# Revit family: NBS_Senator_MeetingPods_EnclaveOne
name_source: partatom
category: Furniture
revit_build: Autodesk Revit 2018 (Build: 20190510_1515(x64)
units: mm (PartAtom-declared; Revit-internal decimal feet)

## family parameters
Always vertical = Yes
Cut with Voids When Loaded = No
Room Calculation Point = No
Shared = No
Work Plane-Based = No

## types (2) — shared parameters
Accessories = Monitor arms, PU desk accessories, desk top accessories, CPU holders, electrical accessories, coat hanger, name plate, A2 dry wipe board with hanger, A3 dry wipe board with hanger
AssetType = Fixed
Category = Pr_40_50_12_53:Meeting pods
DurationUnit = year
EnclaveOneDepth = 1000 mm  [stored 3.28084 ft]
EnclaveOneWidth = 1500 mm  [stored 4.92126 ft]
ExpectedLife = 10
FabricFinishOptions = Plymouth, fairfield, latymer, lancaster, silcoates, silverdale, st andrews, trevelyan, ulster, wellington, wesley, manchester,
Features = Internal frame with multi-layered acoustic foam, levelling adjusters, blazer fabric, outer vertical panels
Finish = Outer vertical panels upholstered in camira, blazer fabric Two tone is standard
FinishOptions = Carini walnut, mocha, autumn, strata oak, maple, highland oak, beech, winter oak, hacienda white, white, light grey, denim, clay, lemon sorbet
FrameMaterial = NBS_Senator_Aluminium_Rigid_Silver
FramesColour = Black, white
IfcExportAs = IfcFurnitureType
IfcExportType = USERDEFINED
InnerPanelMaterial = NBS_Senator_VirginWool_Lancaster
IsBuiltIn = No
ManufacturerName = The Senator Group
ManufacturerURL = www.senator.co.uk
Material = Fabric, metal, plastic
NBSCertification = www.nationalbimlibrary.com/cert/4n0gsb3g
NBSDescription = Meeting pods
NBSReference = 45-35-20/342
NominalDepth = 1000 mm  [stored 3.28084 ft]
NominalLength = 1500 mm  [stored 4.92126 ft]
NominalWidth = 1500 mm  [stored 4.92126 ft]
OuterPanelMaterial = NBS_Senator_VirginWool_Montcrest
ProductInformation = http://www.thesenatorgroup.com
Status = UNSET
Style = Pods
SustainabilityPerformance = 99% recyclable
TableTopMaterial = NBS_Senator_Wood_HighlandOak_2
Uniclass2015Code = Pr_40_50_12_53
Uniclass2015Title = Meeting Pods
Uniclass2015Version = Products v1.16
Version = 1
WarrantyDurationParts = 10
WarrantyDurationUnit = year

## per-type parameters (varying)
| type | BIMObjectName | Description | EnclaveOneHeight | ModelReference | Name | NominalHeight | Size | WarrantyDescription |
| PDEN114 | NBS_Senator_MeetingPods_EnclaveOne_PDEN114 | Enclave One - 1400mm high | 1400 mm  [stored 4.59318 ft] | Pods-EnclaveOne_PDEN114 | MeetingPods_EnclaveOne_PDEN114_Senator | 1400 mm  [stored 4.59318 ft] | 1000 x 1500 x 1400 mm | Senator warrants that its manufactured products are free from manufacturing defects - in materials or workmanship - for a period of ten (10) years on Senator Seating ranges; and fifteen (15) years on Senator Desking ranges - exceptions are listed below. Senator will repair or replace (at Senator’s sole discretion) with comparable free of charge materials / components, any product / component, which fails under normal use in a single shift environment, as a result of a defect in the materials and / or workmanship. |
| PDEN118 | NBS_Senator_MeetingPods_EnclaveOne_PDEN118 | Enclave One - 1800mm high | 1800 mm  [stored 5.90551 ft] | Pods-EnclaveOne_PDEN118 | MeetingPods_EnclaveOne_PDEN118_Senator | 1800 mm  [stored 5.90551 ft] | 1000 x 1500 x 1800 mm | Senator warrants that its manufactured products are free from manufacturing defects - in materials or workmanship - for a period of ten (10) years on Senator Seating ranges; and fifteen (15) years on Senator Desking ranges - exceptions are listed below. Senator will repair or replace (at Senator’s sole discretion) with comparable free of charge materials / components, any product / component, which fails under normal use in a single shift environment, as a result of a defect in the materials and / or workmanship |

note: column(s) folded — value = type name in every type: ModelNumber

note: [stored X ft] marks values corroborated as IEEE doubles in the binary element streams (Revit-internal decimal feet)

## geometry (parser evidence)
native form markers: Sweep x5
no freeform markers — native parametric forms only
